FCSTD DOCUMENT  (FreeCAD 1.0R39319 (Git))
Label: 2BHK_House_Blueprint1
License: All rights reserved
LicenseURL: https://en.wikipedia.org/wiki/All_rights_reserved
objects: App::FeaturePython×26, Part::Part2DObjectPython×23
note: 23 computed .brp shape members not serialized (recipe doc carries the construction recipe); baked Part::Feature solids carry a one-line shape summary decoded from their .brp

FEATURE [Part::Part2DObjectPython] Wire  # Draft 2D object (typed FeaturePython)
  Area = 72000000
  ChamferSize = 0
  Closed = true
  End = (0,0,0)
  FilletRadius = 0
  Length = 36000
  MakeFace = true
  Points = (5) [(0,0,0),(12000,0,0),(12000,6000,0),(0,6000,0),(0,0,0)]
  Start = (0,0,0)
  Subdivisions = 0
FEATURE [Part::Part2DObjectPython] Line  # Draft 2D object (typed FeaturePython)
  Area = 0
  ChamferSize = 0
  Closed = false
  End = (3000,0,0)
  FilletRadius = 0
  Length = 1000
  MakeFace = true
  Points = (2) [(2000,0,0),(3000,0,0)]
  Start = (2000,0,0)
  Subdivisions = 0
FEATURE [Part::Part2DObjectPython] Rectangle  # Draft 2D object (typed FeaturePython)
  Area = 960000
  ChamferSize = 0
  Columns = 1
  FilletRadius = 0
  Height = 1200
  Length = 800
  MakeFace = true
  Placement = pos=(4000,1000,0) rot=(0,0,1;0rad)
  Rows = 1
FEATURE [Part::Part2DObjectPython] Rectangle001  # Draft 2D object (typed FeaturePython)
  Area = 960000
  ChamferSize = 0
  Columns = 1
  FilletRadius = 0
  Height = 1200
  Length = 800
  MakeFace = true
  Placement = pos=(8000,1000,0) rot=(0,0,1;0rad)
  Rows = 1
FEATURE [App::FeaturePython] Dimension  # Draft dimension (typed FeaturePython)
  Diameter = false
  Dimline = (6000,-500,0)
  Direction = (0,0,0)
  Distance = 12000
  End = (12000,-500,0)
  Normal = (0,0,1)
  Start = (0,-500,0)
FEATURE [App::FeaturePython] Dimension001  # Draft dimension (typed FeaturePython)
  Diameter = false
  Dimline = (0,3000,0)
  Direction = (0,0,0)
  Distance = 6000
  End = (0,6000,0)
  Normal = (0,0,1)
  Start = (0,0,0)
FEATURE [App::FeaturePython] Text  # WARN: FeaturePython — macro-defined, semantics opaque (R4)
  Placement = pos=(2500,-500,0) rot=(0,0,1;0rad)
  Text = Main Door
FEATURE [App::FeaturePython] Text001  # WARN: FeaturePython — macro-defined, semantics opaque (R4)
  Placement = pos=(4500,1500,0) rot=(0,0,1;0rad)
  Text = Window
FEATURE [Part::Part2DObjectPython] Wire001  # Draft 2D object (typed FeaturePython)
  Area = 72000000
  ChamferSize = 0
  Closed = true
  End = (0,7000,0)
  FilletRadius = 0
  Length = 36000
  MakeFace = true
  Points = (5) [(0,7000,0),(12000,7000,0),(12000,13000,0),(0,13000,0),(0,7000,0)]
  Start = (0,7000,0)
  Subdivisions = 0
FEATURE [Part::Part2DObjectPython] Rectangle002  # Draft 2D object (typed FeaturePython)
  Area = 18000000
  ChamferSize = 0
  Columns = 1
  FilletRadius = 0
  Height = 3000
  Length = 6000
  MakeFace = true
  Placement = pos=(2000,8000,0) rot=(0,0,1;0rad)
  Rows = 1
FEATURE [Part::Part2DObjectPython] Rectangle003  # Draft 2D object (typed FeaturePython)
  Area = 4e+06
  ChamferSize = 0
  Columns = 1
  FilletRadius = 0
  Height = 2000
  Length = 2000
  MakeFace = true
  Placement = pos=(9000,8000,0) rot=(0,0,1;0rad)
  Rows = 1
FEATURE [Part::Part2DObjectPython] Rectangle004  # Draft 2D object (typed FeaturePython)
  Area = 9000000
  ChamferSize = 0
  Columns = 1
  FilletRadius = 0
  Height = 3000
  Length = 3000
  MakeFace = true
  Placement = pos=(2000,11000,0) rot=(0,0,1;0rad)
  Rows = 1
FEATURE [Part::Part2DObjectPython] Rectangle005  # Draft 2D object (typed FeaturePython)
  Area = 9000000
  ChamferSize = 0
  Columns = 1
  FilletRadius = 0
  Height = 3000
  Length = 3000
  MakeFace = true
  Placement = pos=(6000,11000,0) rot=(0,0,1;0rad)
  Rows = 1
FEATURE [App::FeaturePython] Dimension002  # Draft dimension (typed FeaturePython)
  Diameter = false
  Dimline = (6000,7000,0)
  Direction = (0,0,0)
  Distance = 12000
  End = (12000,7000,0)
  Normal = (0,0,1)
  Start = (0,7000,0)
FEATURE [App::FeaturePython] Dimension003  # Draft dimension (typed FeaturePython)
  Diameter = false
  Dimline = (0,10000,0)
  Direction = (0,0,0)
  Distance = 6000
  End = (0,13000,0)
  Normal = (0,0,1)
  Start = (0,7000,0)
FEATURE [App::FeaturePython] Text002  # WARN: FeaturePython — macro-defined, semantics opaque (R4)
  Placement = pos=(3500,7500,0) rot=(0,0,1;0rad)
  Text = Living Room
FEATURE [App::FeaturePython] Text003  # WARN: FeaturePython — macro-defined, semantics opaque (R4)
  Placement = pos=(9500,7500,0) rot=(0,0,1;0rad)
  Text = Kitchen
FEATURE [App::FeaturePython] Text004  # WARN: FeaturePython — macro-defined, semantics opaque (R4)
  Placement = pos=(2500,11500,0) rot=(0,0,1;0rad)
  Text = Bedroom 1
FEATURE [App::FeaturePython] Text005  # WARN: FeaturePython — macro-defined, semantics opaque (R4)
  Placement = pos=(6500,11500,0) rot=(0,0,1;0rad)
  Text = Bedroom 2
FEATURE [Part::Part2DObjectPython] Wire002  # Draft 2D object (typed FeaturePython)
  Area = 36000000
  ChamferSize = 0
  Closed = true
  End = (0,14000,0)
  FilletRadius = 0
  Length = 30000
  MakeFace = true
  Points = (5) [(0,14000,0),(12000,14000,0),(12000,17000,0),(0,17000,0),(0,14000,0)]
  Start = (0,14000,0)
  Subdivisions = 0
FEATURE [App::FeaturePython] Dimension004  # Draft dimension (typed FeaturePython)
  Diameter = false
  Dimline = (6000,14000,0)
  Direction = (0,0,0)
  Distance = 12000
  End = (12000,14000,0)
  Normal = (0,0,1)
  Start = (0,14000,0)
FEATURE [App::FeaturePython] Dimension005  # Draft dimension (typed FeaturePython)
  Diameter = false
  Dimline = (0,15500,0)
  Direction = (0,0,0)
  Distance = 3000
  End = (0,17000,0)
  Normal = (0,0,1)
  Start = (0,14000,0)
FEATURE [Part::Part2DObjectPython] Line001  # Draft 2D object (typed FeaturePython)
  Area = 0
  ChamferSize = 0
  Closed = false
  End = (0,6000,0)
  FilletRadius = 0
  Length = 6000
  MakeFace = true
  Points = (2) [(0,0,0),(0,6000,0)]
  Start = (0,0,0)
  Subdivisions = 0
FEATURE [App::FeaturePython] Text006  # WARN: FeaturePython — macro-defined, semantics opaque (R4)
  Placement = pos=(0,-500,0) rot=(0,0,1;0rad)
  Text = A
FEATURE [Part::Part2DObjectPython] Line002  # Draft 2D object (typed FeaturePython)
  Area = 0
  ChamferSize = 0
  Closed = false
  End = (1000,6000,0)
  FilletRadius = 0
  Length = 6000
  MakeFace = true
  Points = (2) [(1000,0,0),(1000,6000,0)]
  Start = (1000,0,0)
  Subdivisions = 0
FEATURE [App::FeaturePython] Text007  # WARN: FeaturePython — macro-defined, semantics opaque (R4)
  Placement = pos=(1000,-500,0) rot=(0,0,1;0rad)
  Text = B
FEATURE [Part::Part2DObjectPython] Line003  # Draft 2D object (typed FeaturePython)
  Area = 0
  ChamferSize = 0
  Closed = false
  End = (2000,6000,0)
  FilletRadius = 0
  Length = 6000
  MakeFace = true
  Points = (2) [(2000,0,0),(2000,6000,0)]
  Start = (2000,0,0)
  Subdivisions = 0
FEATURE [App::FeaturePython] Text008  # WARN: FeaturePython — macro-defined, semantics opaque (R4)
  Placement = pos=(2000,-500,0) rot=(0,0,1;0rad)
  Text = C
FEATURE [Part::Part2DObjectPython] Line004  # Draft 2D object (typed FeaturePython)
  Area = 0
  ChamferSize = 0
  Closed = false
  End = (3000,6000,0)
  FilletRadius = 0
  Length = 6000
  MakeFace = true
  Points = (2) [(3000,0,0),(3000,6000,0)]
  Start = (3000,0,0)
  Subdivisions = 0
FEATURE [App::FeaturePython] Text009  # WARN: FeaturePython — macro-defined, semantics opaque (R4)
  Placement = pos=(3000,-500,0) rot=(0,0,1;0rad)
  Text = D
FEATURE [Part::Part2DObjectPython] Line005  # Draft 2D object (typed FeaturePython)
  Area = 0
  ChamferSize = 0
  Closed = false
  End = (4000,6000,0)
  FilletRadius = 0
  Length = 6000
  MakeFace = true
  Points = (2) [(4000,0,0),(4000,6000,0)]
  Start = (4000,0,0)
  Subdivisions = 0
FEATURE [App::FeaturePython] Text010  # WARN: FeaturePython — macro-defined, semantics opaque (R4)
  Placement = pos=(4000,-500,0) rot=(0,0,1;0rad)
  Text = E
FEATURE [Part::Part2DObjectPython] Line006  # Draft 2D object (typed FeaturePython)
  Area = 0
  ChamferSize = 0
  Closed = false
  End = (5000,6000,0)
  FilletRadius = 0
  Length = 6000
  MakeFace = true
  Points = (2) [(5000,0,0),(5000,6000,0)]
  Start = (5000,0,0)
  Subdivisions = 0
FEATURE [App::FeaturePython] Text011  # WARN: FeaturePython — macro-defined, semantics opaque (R4)
  Placement = pos=(5000,-500,0) rot=(0,0,1;0rad)
  Text = F
FEATURE [Part::Part2DObjectPython] Line007  # Draft 2D object (typed FeaturePython)
  Area = 0
  ChamferSize = 0
  Closed = false
  End = (6000,6000,0)
  FilletRadius = 0
  Length = 6000
  MakeFace = true
  Points = (2) [(6000,0,0),(6000,6000,0)]
  Start = (6000,0,0)
  Subdivisions = 0
FEATURE [App::FeaturePython] Text012  # WARN: FeaturePython — macro-defined, semantics opaque (R4)
  Placement = pos=(6000,-500,0) rot=(0,0,1;0rad)
  Text = G
FEATURE [Part::Part2DObjectPython] Line008  # Draft 2D object (typed FeaturePython)
  Area = 0
  ChamferSize = 0
  Closed = false
  End = (7000,6000,0)
  FilletRadius = 0
  Length = 6000
  MakeFace = true
  Points = (2) [(7000,0,0),(7000,6000,0)]
  Start = (7000,0,0)
  Subdivisions = 0
FEATURE [App::FeaturePython] Text013  # WARN: FeaturePython — macro-defined, semantics opaque (R4)
  Placement = pos=(7000,-500,0) rot=(0,0,1;0rad)
  Text = H
FEATURE [Part::Part2DObjectPython] Line009  # Draft 2D object (typed FeaturePython)
  Area = 0
  ChamferSize = 0
  Closed = false
  End = (8000,6000,0)
  FilletRadius = 0
  Length = 6000
  MakeFace = true
  Points = (2) [(8000,0,0),(8000,6000,0)]
  Start = (8000,0,0)
  Subdivisions = 0
FEATURE [App::FeaturePython] Text014  # WARN: FeaturePython — macro-defined, semantics opaque (R4)
  Placement = pos=(8000,-500,0) rot=(0,0,1;0rad)
  Text = I
FEATURE [Part::Part2DObjectPython] Line010  # Draft 2D object (typed FeaturePython)
  Area = 0
  ChamferSize = 0
  Closed = false
  End = (9000,6000,0)
  FilletRadius = 0
  Length = 6000
  MakeFace = true
  Points = (2) [(9000,0,0),(9000,6000,0)]
  Start = (9000,0,0)
  Subdivisions = 0
FEATURE [App::FeaturePython] Text015  # WARN: FeaturePython — macro-defined, semantics opaque (R4)
  Placement = pos=(9000,-500,0) rot=(0,0,1;0rad)
  Text = J
FEATURE [Part::Part2DObjectPython] Line011  # Draft 2D object (typed FeaturePython)
  Area = 0
  ChamferSize = 0
  Closed = false
  End = (10000,6000,0)
  FilletRadius = 0
  Length = 6000
  MakeFace = true
  Points = (2) [(10000,0,0),(10000,6000,0)]
  Start = (10000,0,0)
  Subdivisions = 0
FEATURE [App::FeaturePython] Text016  # WARN: FeaturePython — macro-defined, semantics opaque (R4)
  Placement = pos=(10000,-500,0) rot=(0,0,1;0rad)
  Text = K
FEATURE [Part::Part2DObjectPython] Line012  # Draft 2D object (typed FeaturePython)
  Area = 0
  ChamferSize = 0
  Closed = false
  End = (11000,6000,0)
  FilletRadius = 0
  Length = 6000
  MakeFace = true
  Points = (2) [(11000,0,0),(11000,6000,0)]
  Start = (11000,0,0)
  Subdivisions = 0
FEATURE [App::FeaturePython] Text017  # WARN: FeaturePython — macro-defined, semantics opaque (R4)
  Placement = pos=(11000,-500,0) rot=(0,0,1;0rad)
  Text = L
FEATURE [Part::Part2DObjectPython] Line013  # Draft 2D object (typed FeaturePython)
  Area = 0
  ChamferSize = 0
  Closed = false
  End = (12000,6000,0)
  FilletRadius = 0
  Length = 6000
  MakeFace = true
  Points = (2) [(12000,0,0),(12000,6000,0)]
  Start = (12000,0,0)
  Subdivisions = 0
FEATURE [App::FeaturePython] Text018  # WARN: FeaturePython — macro-defined, semantics opaque (R4)
  Placement = pos=(12000,-500,0) rot=(0,0,1;0rad)
  Text = M
FEATURE [App::FeaturePython] Text019  # WARN: FeaturePython — macro-defined, semantics opaque (R4)
  Placement = pos=(10000,17500,0) rot=(0,0,1;0rad)
  Text = 2BHK House Blueprint | Scale: 1:100 | Date: 2024-09-16
